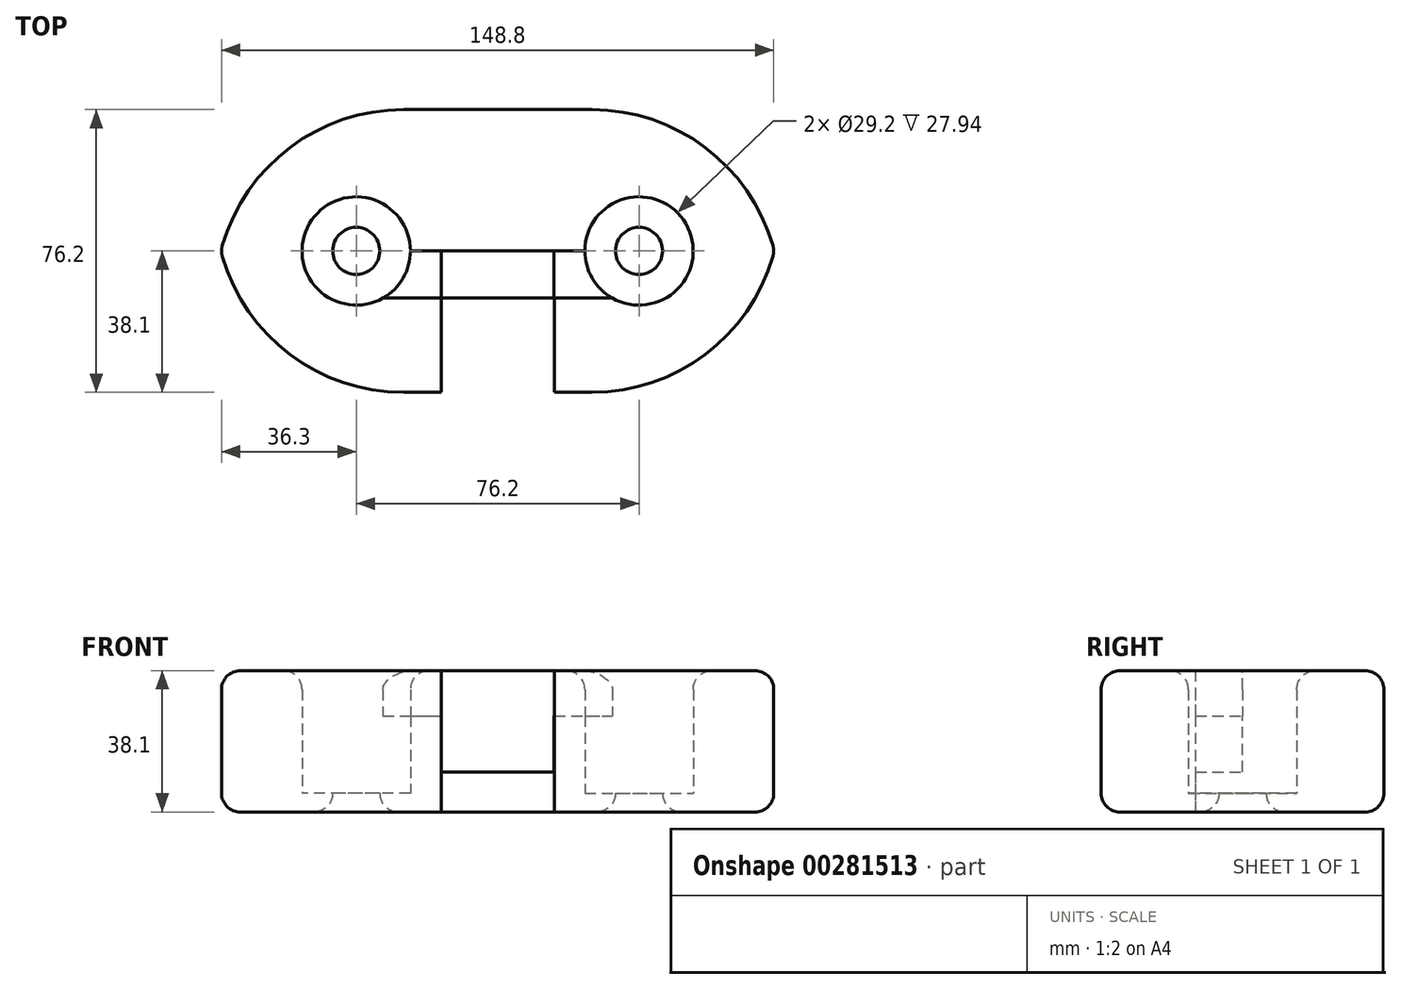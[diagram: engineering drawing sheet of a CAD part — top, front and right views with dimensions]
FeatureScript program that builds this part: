
annotation { "Feature Type Name" : "Feature", "Feature Type Description" : "" }
export const myFeature = defineFeature(function(context is Context, id is Id, definition is map)
    precondition{}
    {
        {
            var Q0;
            Q0=qCreatedBy(makeId("Top.planeOp"),FACE);
            var sketch = newSketch(context, id + "F0", { "sketchPlane" : qUnion([Q0])});
            skLineSegment(sketch, "E0.bottom", {"start": v(-76.2, 38.1) * mm, "end": v(76.2, 38.1) * mm});
            skLineSegment(sketch, "E0.top", {"start": v(-76.2, -38.1) * mm, "end": v(76.2, -38.1) * mm});
            skLineSegment(sketch, "E0.left", {"start": v(-76.2, 38.1) * mm, "end": v(-76.2, -38.1) * mm});
            skLineSegment(sketch, "E0.right", {"start": v(76.2, 38.1) * mm, "end": v(76.2, -38.1) * mm});
            skPoint(sketch, "E0.middle", {"position": v(0, 0) * mm});
            skSolve(sketch);
        }
        {
            var Q0;
            Q0 = qSketchRegion(id + "F0", true);
            extrude(context, id + "F1", {"entities" : qUnion([Q0]), "depth" : 38.1 * mm});
        }
        {
            var Q0;
            Q0=qCreatedBy(makeId("Top.planeOp"),FACE);
            var sketch = newSketch(context, id + "F2", { "sketchPlane" : qUnion([Q0])});
            skLineSegment(sketch, "E1", {"start": v(0, 0) * mm, "end": v(-76.2, 0) * mm, "construction": true});
            skLineSegment(sketch, "E2", {"start": v(0, 0) * mm, "end": v(-38.1, 0) * mm, "construction": true});
            skLineSegment(sketch, "E3", {"start": v(0, 0) * mm, "end": v(76.2, 0) * mm, "construction": true});
            skLineSegment(sketch, "E4", {"start": v(0, 0) * mm, "end": v(38.1, 0) * mm, "construction": true});
            skCircle(sketch, "E5", {"center": v(38.1, 0) * mm, "radius": 14.6 * mm});
            skCircle(sketch, "E6", {"center": v(-38.1, 0) * mm, "radius": 14.6 * mm});
            skSolve(sketch);
        }
        {
            var Q0;
            Q0 = qSketchRegion(id + "F2", true);
            extrude(context, id + "F3", {"entities" : qUnion([Q0]), "operationType" : NewBodyOperationType.REMOVE, "depth" : 38.1 * mm});
        }
        {
            var Q0;
            Q0=qCreatedBy(makeId("Top.planeOp"),FACE);
            var sketch = newSketch(context, id + "F4", { "sketchPlane" : qUnion([Q0])});
            skLineSegment(sketch, "E7", {"start": v(0, 0) * mm, "end": v(-76.2, 0) * mm, "construction": true});
            skLineSegment(sketch, "E8", {"start": v(0, 0) * mm, "end": v(-38.1, 0) * mm, "construction": true});
            skCircle(sketch, "E9", {"center": v(-38.1, 0) * mm, "radius": 6.35 * mm});
            skCircle(sketch, "E10.MirrorC", {"center": v(38.1, 0) * mm, "radius": 6.35 * mm});
            skCircle(sketch, "E11", {"center": v(-38.1, 0) * mm, "radius": 14.6 * mm});
            skCircle(sketch, "E12", {"center": v(38.1, 0) * mm, "radius": 14.6 * mm});
            skLineSegment(sketch, "E13", {"start": v(37.83, 6.34) * mm, "end": v(37.83, 14.6) * mm});
            skLineSegment(sketch, "E14", {"start": v(44.45, 0) * mm, "end": v(52.7, 0) * mm});
            skLineSegment(sketch, "E15", {"start": v(37.83, -6.34) * mm, "end": v(37.83, -14.6) * mm});
            skLineSegment(sketch, "E16", {"start": v(31.75, 0) * mm, "end": v(23.5, 0) * mm});
            skSolve(sketch);
        }
        {
            var Q0;
            Q0=makeQuery(id+"F4.imprint","IMPRINT",FACE,{"disambiguationData":[TD([[makeQuery(id+"F4.imprint","IMPRINT",EDGE,{"derivedFrom":sQuery(id+"F4.wireOp",EDGE,"E9")}),-1.0]])]});
            extrude(context, id + "F5", {"entities" : qUnion([Q0]), "operationType" : NewBodyOperationType.ADD, "depth" : 5.08 * mm});
        }
        {
            var Q0;
            Q0=makeQuery(id+"F1.opExtrude","SWEPT_BODY",BODY,{"disambiguationData":[OSD([sQuery(id+"F0.wireOp",EDGE,"E0.bottom"),sQuery(id+"F0.wireOp",EDGE,"E0.top"),sQuery(id+"F0.wireOp",EDGE,"E0.left"),sQuery(id+"F0.wireOp",EDGE,"E0.right")])]});
            var Q1;
            Q1=qCreatedBy(makeId("Right.planeOp"),FACE);
            mirror(context, id + "F6", {"operationType" : NewBodyOperationType.ADD, "entities" : qUnion([Q0]), "mirrorPlane" : qUnion([Q1])});
        }
        {
            var Q0;
            Q0=qCreatedBy(makeId("Front.planeOp"),FACE);
            var sketch = newSketch(context, id + "F7", { "sketchPlane" : qUnion([Q0])});
            skLineSegment(sketch, "E17", {"start": v(0, 0) * mm, "end": v(0, 38.1) * mm, "construction": true});
            skLineSegment(sketch, "E18", {"start": v(0, 0) * mm, "end": v(0, 19.05) * mm, "construction": true});
            skLineSegment(sketch, "E19", {"start": v(0, 19.05) * mm, "end": v(76.2, 19.05) * mm, "construction": true});
            skLineSegment(sketch, "E20", {"start": v(0, 19.05) * mm, "end": v(-76.2, 19.05) * mm, "construction": true});
            skLineSegment(sketch, "E21", {"start": v(0, 19.05) * mm, "end": v(-38.1, 19.05) * mm, "construction": true});
            skLineSegment(sketch, "E22", {"start": v(0, 19.05) * mm, "end": v(38.1, 19.05) * mm, "construction": true});
            skLineSegment(sketch, "E23", {"start": v(0, 19.05) * mm, "end": v(0, 9.53) * mm, "construction": true});
            skLineSegment(sketch, "E24", {"start": v(0, 19.05) * mm, "end": v(0, 28.58) * mm, "construction": true});
            skLineSegment(sketch, "E25.bottom", {"start": v(15.24, 10.8) * mm, "end": v(-15.24, 10.8) * mm});
            skLineSegment(sketch, "E25.top", {"start": v(15.24, 27.3) * mm, "end": v(-15.24, 27.3) * mm});
            skLineSegment(sketch, "E25.left", {"start": v(15.24, 10.8) * mm, "end": v(15.24, 27.3) * mm});
            skLineSegment(sketch, "E25.right", {"start": v(-15.24, 10.8) * mm, "end": v(-15.24, 27.3) * mm});
            skPoint(sketch, "E25.middle", {"position": v(0, 19.05) * mm});
            skSolve(sketch);
        }
        {
            var Q0;
            Q0 = qSketchRegion(id + "F7", true);
            extrude(context, id + "F8", {"entities" : qUnion([Q0]), "operationType" : NewBodyOperationType.REMOVE, "depth" : 38.1 * mm});
        }
        {
            var Q0;
            Q0=makeQuery(id+"F1.opExtrude","SWEPT_EDGE",EDGE,{"disambiguationData":[OSD([sQuery(id+"F0.wireOp",EDGE,"E0.bottom"),sQuery(id+"F0.wireOp",EDGE,"E0.left")])]});
            var Q1;
            Q1=makeQuery(id+"F1.opExtrude","SWEPT_EDGE",EDGE,{"disambiguationData":[OSD([sQuery(id+"F0.wireOp",EDGE,"E0.top"),sQuery(id+"F0.wireOp",EDGE,"E0.left")])]});
            var Q2;
            Q2=makeQuery(id+"F1.opExtrude","SWEPT_EDGE",EDGE,{"disambiguationData":[OSD([sQuery(id+"F0.wireOp",EDGE,"E0.bottom"),sQuery(id+"F0.wireOp",EDGE,"E0.right")])]});
            var Q3;
            Q3=makeQuery(id+"F1.opExtrude","SWEPT_EDGE",EDGE,{"disambiguationData":[OSD([sQuery(id+"F0.wireOp",EDGE,"E0.top"),sQuery(id+"F0.wireOp",EDGE,"E0.right")])]});
            fillet(context, id + "F9", {"entities" : qUnion([Q0, Q1, Q2, Q3]), "radius" : 50.8 * mm, "tangentPropagation" : true, "allowEdgeOverflow" : false});
        }
        {
            var Q0;
            Q0=makeQuery(id+"F1.opExtrude","CAP_FACE",FACE,{"disambiguationData":[OSD([sQuery(id+"F0.wireOp",EDGE,"E0.bottom"),sQuery(id+"F0.wireOp",EDGE,"E0.top"),sQuery(id+"F0.wireOp",EDGE,"E0.left"),sQuery(id+"F0.wireOp",EDGE,"E0.right")])],"isStart":false});
            var Q1;
            {var subQ0=makeQuery(id+"F5.boolean.opBoolean","MERGE",FACE,{"derivedFrom":[makeQuery(id+"F1.opExtrude","CAP_FACE",FACE,{"disambiguationData":[OSD([sQuery(id+"F0.wireOp",EDGE,"E0.bottom"),sQuery(id+"F0.wireOp",EDGE,"E0.top"),sQuery(id+"F0.wireOp",EDGE,"E0.left"),sQuery(id+"F0.wireOp",EDGE,"E0.right")])],"isStart":true}),makeQuery(id+"F5.opExtrude","CAP_FACE",FACE,{"disambiguationData":[OSD([sQuery(id+"F4.wireOp",EDGE,"E9"),sQuery(id+"F4.wireOp",EDGE,"E11")])],"isStart":true})]});Q1=makeQuery(id+"F6.boolean.opBoolean","MERGE",FACE,{"derivedFrom":[subQ0,makeQuery(id+"F6.opPattern","COPY",FACE,{"derivedFrom":subQ0,"instanceName":"1"})]});}
            var Q2;
            {var subQ0=sQuery(id+"F0.wireOp",EDGE,"E0.right");Q2=makeQuery(id+"F9.opFillet","BLEND_EDGE",EDGE,{"blendedFrom":[makeQuery(id+"F1.opExtrude","SWEPT_EDGE",EDGE,{"disambiguationData":[OSD([sQuery(id+"F0.wireOp",EDGE,"E0.bottom"),subQ0])]}),makeQuery(id+"F1.opExtrude","SWEPT_EDGE",EDGE,{"disambiguationData":[OSD([sQuery(id+"F0.wireOp",EDGE,"E0.top"),subQ0])]})],"blendedInto":[]});}
            var Q3;
            {var subQ0=sQuery(id+"F0.wireOp",EDGE,"E0.left");Q3=makeQuery(id+"F9.opFillet","BLEND_EDGE",EDGE,{"blendedFrom":[makeQuery(id+"F1.opExtrude","SWEPT_EDGE",EDGE,{"disambiguationData":[OSD([sQuery(id+"F0.wireOp",EDGE,"E0.bottom"),subQ0])]}),makeQuery(id+"F1.opExtrude","SWEPT_EDGE",EDGE,{"disambiguationData":[OSD([sQuery(id+"F0.wireOp",EDGE,"E0.top"),subQ0])]})],"blendedInto":[]});}
            fillet(context, id + "F10", {"entities" : qUnion([Q0, Q1, Q2, Q3]), "radius" : 5.08 * mm, "tangentPropagation" : true, "allowEdgeOverflow" : false});
        }
        {
            var Q0;
            Q0=qCreatedBy(makeId("Front.planeOp"),FACE);
            var sketch = newSketch(context, id + "F11", { "sketchPlane" : qUnion([Q0])});
            skLineSegment(sketch, "E26", {"start": v(0, 0) * mm, "end": v(0, 38.1) * mm, "construction": true});
            skLineSegment(sketch, "E27", {"start": v(0, 38.1) * mm, "end": v(0, 0) * mm, "construction": true});
            skLineSegment(sketch, "E28", {"start": v(-15.22, 27.34) * mm, "end": v(-15.22, 38.1) * mm, "construction": true});
            skLineSegment(sketch, "E29.bottom", {"start": v(-15.22, 38.1) * mm, "end": v(15.19, 38.1) * mm});
            skLineSegment(sketch, "E29.top", {"start": v(-15.22, 27.34) * mm, "end": v(15.19, 27.34) * mm});
            skLineSegment(sketch, "E29.left", {"start": v(-15.22, 38.1) * mm, "end": v(-15.22, 27.34) * mm});
            skLineSegment(sketch, "E30", {"start": v(15.19, 38.1) * mm, "end": v(15.19, 27.34) * mm});
            skSolve(sketch);
        }
        {
            var Q0;
            Q0 = qSketchRegion(id + "F11", true);
            var Q1;
            Q1 = qConstructionFilter(qBodyType(qCreatedBy(id + "F11" ,EDGE), BodyType.WIRE), ConstructionObject.NO);
            extrude(context, id + "F12", {"entities" : qUnion([Q0]), "operationType" : NewBodyOperationType.REMOVE, "surfaceEntities" : qUnion([Q1]), "depth" : 38.1 * mm});
        }
        {
            var Q0;
            Q0=qCreatedBy(makeId("Front.planeOp"),FACE);
            var sketch = newSketch(context, id + "F13", { "sketchPlane" : qUnion([Q0])});
            skLineSegment(sketch, "E31", {"start": v(0, 38.1) * mm, "end": v(38.1, 38.1) * mm, "construction": true});
            skLineSegment(sketch, "E32", {"start": v(0, 38.1) * mm, "end": v(19.05, 38.1) * mm, "construction": true});
            skLineSegment(sketch, "E33.bottom", {"start": v(38.1, 38.1) * mm, "end": v(0, 38.1) * mm});
            skLineSegment(sketch, "E33.top", {"start": v(38.1, 25.94) * mm, "end": v(0, 25.94) * mm});
            skLineSegment(sketch, "E33.left", {"start": v(38.1, 38.1) * mm, "end": v(38.1, 25.94) * mm});
            skLineSegment(sketch, "E33.right", {"start": v(0, 38.1) * mm, "end": v(0, 25.94) * mm, "construction": true});
            skLineSegment(sketch, "E34.MirrorCS", {"start": v(-38.1, 25.94) * mm, "end": v(0, 25.94) * mm});
            skLineSegment(sketch, "E35.MirrorCS", {"start": v(-38.1, 38.1) * mm, "end": v(0, 38.1) * mm});
            skLineSegment(sketch, "E36.MirrorCS", {"start": v(-38.1, 38.1) * mm, "end": v(-38.1, 25.94) * mm});
            skSolve(sketch);
        }
        {
            var Q0;
            Q0=makeQuery(id+"F13.imprint","IMPRINT",FACE,{"disambiguationData":[TD([[makeQuery(id+"F13.imprint","IMPRINT",EDGE,{"derivedFrom":sQuery(id+"F13.wireOp",EDGE,"E33.bottom")}),1.0]])]});
            extrude(context, id + "F14", {"entities" : qUnion([Q0]), "operationType" : NewBodyOperationType.REMOVE, "depth" : 12.7 * mm});
        }
        {
            var Q0;
            Q0=qCreatedBy(makeId("Top.planeOp"),FACE);
            var sketch = newSketch(context, id + "F15", { "sketchPlane" : qUnion([Q0])});
            skLineSegment(sketch, "E37", {"start": v(0, 0) * mm, "end": v(0, -38.1) * mm, "construction": true});
            skLineSegment(sketch, "E38", {"start": v(0, 0) * mm, "end": v(0, -19.05) * mm, "construction": true});
            skLineSegment(sketch, "E39", {"start": v(0, -19.05) * mm, "end": v(15.13, -19.05) * mm, "construction": true});
            skLineSegment(sketch, "E40", {"start": v(0, -19.05) * mm, "end": v(-15.24, -19.05) * mm, "construction": true});
            skLineSegment(sketch, "E41", {"start": v(0, -19.05) * mm, "end": v(0, -38.1) * mm, "construction": true});
            skLineSegment(sketch, "E42", {"start": v(0, -19.05) * mm, "end": v(0, -12.7) * mm, "construction": true});
            skLineSegment(sketch, "E43", {"start": v(0, -12.7) * mm, "end": v(-15.24, -12.7) * mm, "construction": true});
            skLineSegment(sketch, "E44.bottom", {"start": v(-15.24, -12.7) * mm, "end": v(15.27, -12.7) * mm});
            skLineSegment(sketch, "E44.top", {"start": v(-15.24, -38.1) * mm, "end": v(15.27, -38.1) * mm});
            skLineSegment(sketch, "E44.left", {"start": v(-15.24, -12.7) * mm, "end": v(-15.24, -38.1) * mm});
            skLineSegment(sketch, "E44.right", {"start": v(15.27, -12.7) * mm, "end": v(15.27, -38.1) * mm});
            skSolve(sketch);
        }
        {
            var Q0;
            Q0 = qSketchRegion(id + "F15", true);
            extrude(context, id + "F16", {"entities" : qUnion([Q0]), "operationType" : NewBodyOperationType.REMOVE, "depth" : 38.1 * mm});
        }
    });
